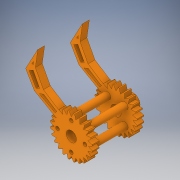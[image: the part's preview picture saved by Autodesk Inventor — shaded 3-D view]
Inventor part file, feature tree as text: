
AUTODESK INVENTOR PART (.ipt)
format: ipt  version: 2017 (Build 210142000, 142)  size: 631,808 bytes
history: native  units: in
note: dims shown in document units (in); Inventor stores cm internally (conversion verified against a paired STEP export)
features: extrude x27, sketch x27
ambient origin geometry x8: Origin, YZ Plane, XZ Plane, XY Plane, X Axis, Y Axis, Z Axis, Center Point
bodies: Solid1 (feature_tree)
feature tree (54):
  extrude  "Extrusion1"  Depth=0.5in
  extrude  "Extrusion2"  TaperAngle=150.0deg  [1 undecoded]
  extrude  "Extrusion3"  Depth=0.2in TaperAngle=0.0deg
  extrude  "Extrusion4"  TaperAngle=30.0deg  [1 undecoded]
  extrude  "Extrusion5"  TaperAngle=60.0deg  [1 undecoded]
  extrude  "Extrusion6"  Depth=0.2in TaperAngle=0.0deg
  extrude  "Extrusion7"  Depth=0.2in
  extrude  "Extrusion8"  Depth=0.2in TaperAngle=0.0deg
  extrude  "Extrusion9"  Depth=0.2in TaperAngle=0.0deg
  extrude  "Extrusion10"  Depth=0.4in
  extrude  "Extrusion11"  Depth=0.4in
  extrude  "Extrusion12"  Depth=0.4in
  extrude  "Extrusion13"  Depth=0.4in
  extrude  "Extrusion14"  Depth=0.2in TaperAngle=0.0deg
  extrude  "Extrusion15"  TaperAngle=60.0deg  [1 undecoded]
  extrude  "Extrusion16"  Depth=0.5in
  extrude  "Extrusion17"  Depth=0.2in TaperAngle=0.0deg
  extrude  "Extrusion18"  TaperAngle=135.0deg  [1 undecoded]
  extrude  "Extrusion19"  TaperAngle=45.0deg  [1 undecoded]
  extrude  "Extrusion20"  TaperAngle=135.0deg  [1 undecoded]
  extrude  "Extrusion21"  Depth=0.2in
  extrude  "Extrusion22"  Depth=1.1in TaperAngle=0.0deg
  extrude  "Extrusion23"  Depth=0.2in TaperAngle=0.0deg
  extrude  "Extrusion24"  Depth=0.2in TaperAngle=0.0deg
  extrude  "Extrusion25"  Depth=0.2in TaperAngle=0.0deg
  extrude  "Extrusion26"  Depth=0.2in TaperAngle=0.0deg
  extrude  "Extrusion27"  Depth=0.2in TaperAngle=0.0deg
  sketch  "Sketch1"  dims[d0=0.5in d1=0.5in]
  sketch  "Sketch2"  dims[d2=15.0deg d3=150.0deg]
  sketch  "Sketch3"  dims[d4=30.0deg d5=0.2in d6=0.0in]
  sketch  "Sketch4"  dims[d7=0.5in d8=30.0deg]
  sketch  "Sketch5"  dims[d9=60.0deg d10=60.0deg]
  sketch  "Sketch6"  dims[d11=0.2in d12=0.0in d13=0.2in d14=0.0in]
  sketch  "Sketch7"  dims[d15=0.2in d16=0.0in d17=1.0in]
  sketch  "Sketch8"  dims[d18=0.2in d19=0.0in d20=0.2in d21=0.0in]
  sketch  "Sketch9"  dims[d22=0.3in d23=0.2in d24=0.0in]
  sketch  "Sketch10"  dims[d25=0.2in d26=0.0in d27=0.4in]
  sketch  "Sketch11"  dims[d28=0.11in d29=0.4in]
  sketch  "Sketch12"  dims[d30=0.11in d31=0.4in]
  sketch  "Sketch13"  dims[d32=0.4in d33=0.11in]
  sketch  "Sketch14"  dims[d34=0.11in d35=0.2in d36=0.0in]
  sketch  "Sketch15"  dims[d37=1.5in d38=60.0deg]
  sketch  "Sketch16"  dims[d39=30.0deg d40=0.5in]
  sketch  "Sketch17"  dims[d41=150.0deg d42=0.2in d43=0.0in]
  sketch  "Sketch18"  dims[d44=0.2in d45=0.0in d46=135.0deg]
  sketch  "Sketch19"  dims[d47=0.2in d48=45.0deg]
  sketch  "Sketch20"  dims[d49=45.0deg d50=135.0deg]
  sketch  "Sketch21"  dims[d51=0.2in d52=0.2in]
  sketch  "Sketch22"  dims[d53=0.2in d54=1.1in d55=0.0in]
  sketch  "Sketch23"  dims[d56=30.0deg d57=0.2in d58=0.0in]
  sketch  "Sketch24"  dims[d59=0.2in d60=0.0in d61=0.2in d62=0.0in]
  sketch  "Sketch25"  dims[d63=0.2in d64=0.0in d65=0.2in d66=0.0in]
  sketch  "Sketch26"  dims[d67=0.2in d68=0.0in d69=0.2in d70=0.0in]
  sketch  "Sketch27"  dims[d71=0.3in d72=0.2in d73=0.0in d74=0.2in d75=0.0in d76=2.0in d77=0.0in d78=2.0in d79=0.0in d80=2.0in d81=0.0in d82=0.6in d83=0.05in d84=0.0in d85=0.4in d86=0.25in d87=0.0in d88=0.3in d89=1.0in d90=0.0in]
note: 7 required parameter values undecoded (feature->parameter linkage not recoverable at this tier; creation-order binding heuristic only, values carry confidence <= 0.55)
